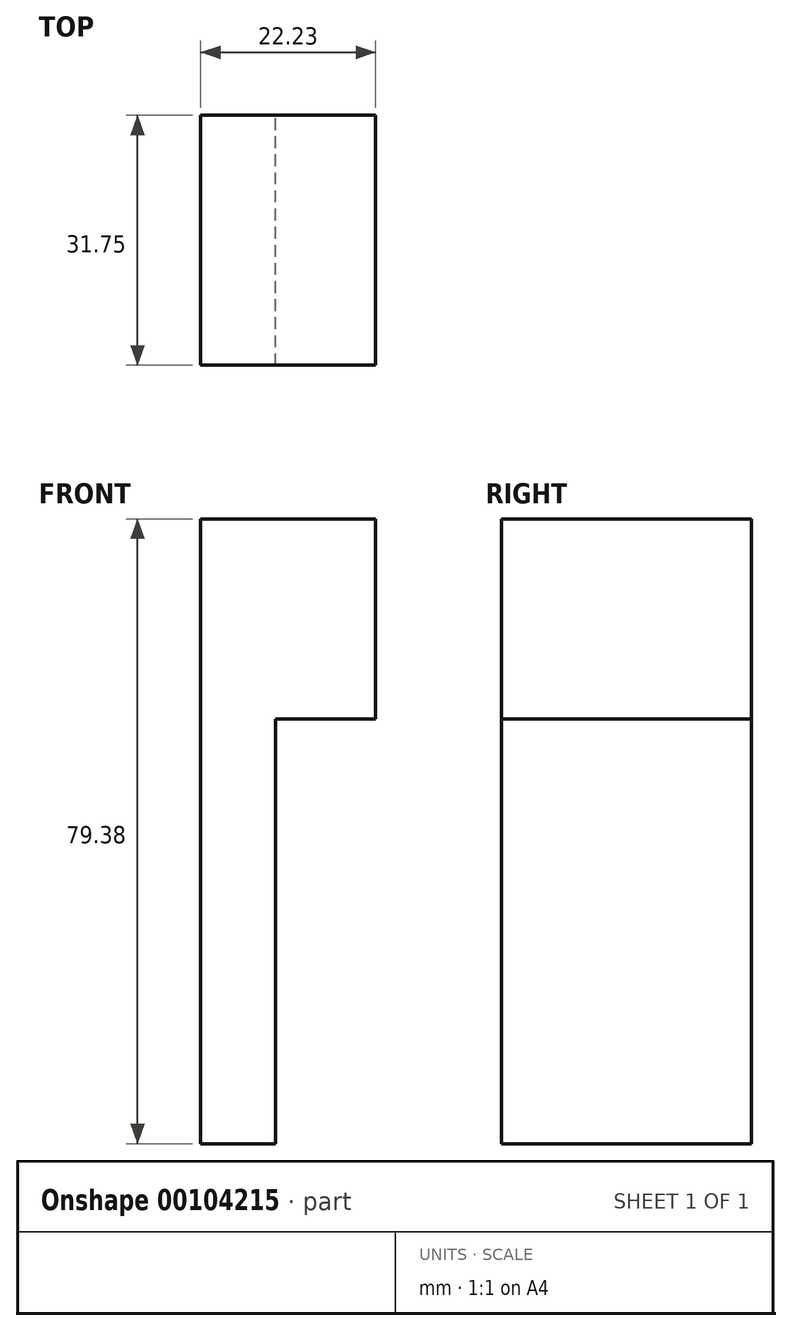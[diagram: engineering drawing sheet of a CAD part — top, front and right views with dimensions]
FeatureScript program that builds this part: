
annotation { "Feature Type Name" : "Feature", "Feature Type Description" : "" }
export const myFeature = defineFeature(function(context is Context, id is Id, definition is map)
    precondition{}
    {
        {
            var Q0;
            Q0=qCreatedBy(makeId("Front.planeOp"),FACE);
            var sketch = newSketch(context, id + "F0", { "sketchPlane" : qUnion([Q0])});
            skLineSegment(sketch, "E0", {"start": v(0, 0) * mm, "end": v(-9.52, 0) * mm});
            skLineSegment(sketch, "E1", {"start": v(-9.52, 0) * mm, "end": v(-9.52, 79.38) * mm});
            skLineSegment(sketch, "E2.bottom", {"start": v(-9.53, 79.38) * mm, "end": v(0, 79.38) * mm});
            skLineSegment(sketch, "E2.top", {"start": v(-9.52, 0) * mm, "end": v(0, 0) * mm});
            skLineSegment(sketch, "E2.left", {"start": v(-9.52, 79.38) * mm, "end": v(-9.52, 0) * mm});
            skLineSegment(sketch, "E2.right", {"start": v(0, 79.38) * mm, "end": v(0, 0) * mm});
            skSolve(sketch);
        }
        {
            var Q0;
            Q0=makeQuery(id+"F0.imprint","IMPRINT",FACE,{"disambiguationData":[TD([[makeQuery(id+"F0.imprint","IMPRINT",EDGE,{"derivedFrom":sQuery(id+"F0.wireOp",EDGE,"E2.bottom")}),-1.0]])]});
            extrude(context, id + "F1", {"entities" : qUnion([Q0]), "oppositeDirection" : true, "depth" : 31.75 * mm});
        }
        {
            var Q0;
            Q0=makeQuery(id+"F1.opExtrude","SWEPT_FACE",FACE,{"disambiguationData":[OSD([sQuery(id+"F0.wireOp",EDGE,"E2.right")])]});
            var sketch = newSketch(context, id + "F2", { "sketchPlane" : qUnion([Q0])});
            skLineSegment(sketch, "E3.bottom", {"start": v(0, 79.38) * mm, "end": v(31.75, 79.38) * mm});
            skLineSegment(sketch, "E3.top", {"start": v(0, 53.98) * mm, "end": v(31.75, 53.98) * mm});
            skLineSegment(sketch, "E3.left", {"start": v(0, 79.38) * mm, "end": v(0, 53.98) * mm});
            skLineSegment(sketch, "E3.right", {"start": v(31.75, 79.38) * mm, "end": v(31.75, 53.98) * mm});
            skSolve(sketch);
        }
        {
            var Q0;
            Q0=makeQuery(id+"F2.imprint","IMPRINT",FACE,{"disambiguationData":[TD([[makeQuery(id+"F2.imprint","IMPRINT",EDGE,{"derivedFrom":sQuery(id+"F2.wireOp",EDGE,"E3.bottom")}),1.0]])]});
            extrude(context, id + "F3", {"entities" : qUnion([Q0]), "operationType" : NewBodyOperationType.ADD, "depth" : 12.7 * mm});
        }
    });
